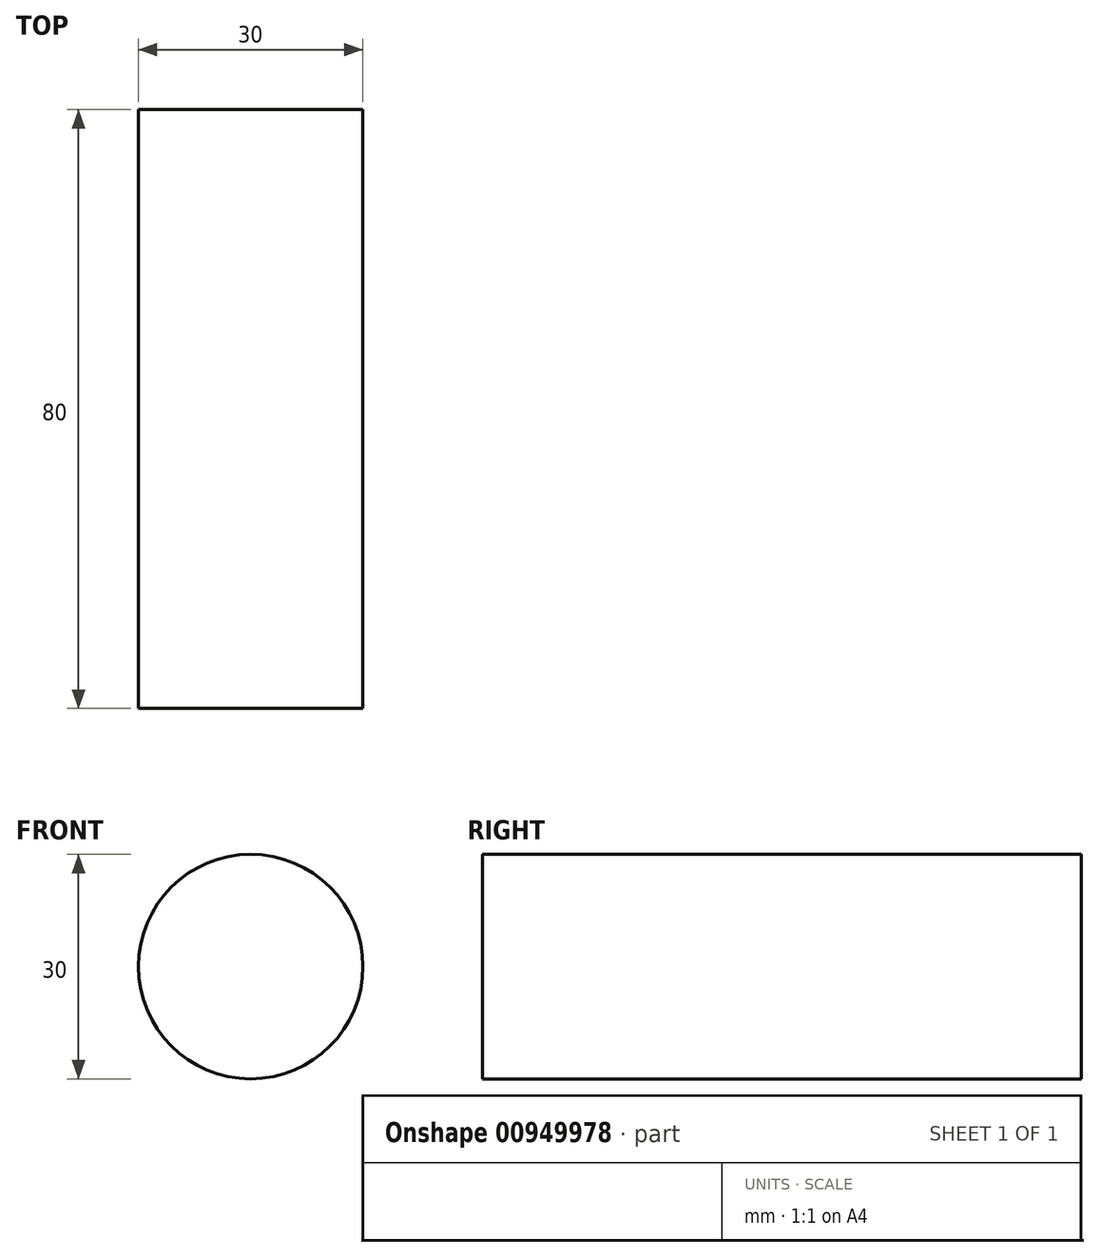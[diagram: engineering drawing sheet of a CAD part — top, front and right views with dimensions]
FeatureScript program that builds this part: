
annotation { "Feature Type Name" : "Feature", "Feature Type Description" : "" }
export const myFeature = defineFeature(function(context is Context, id is Id, definition is map)
    precondition{}
    {
        {
            var Q0;
            Q0=qCreatedBy(makeId("Front.planeOp"),FACE);
            var sketch = newSketch(context, id + "F0", { "sketchPlane" : qUnion([Q0])});
            skCircle(sketch, "E0", {"center": v(0, 0) * mm, "radius": 15 * mm});
            skSolve(sketch);
        }
        {
            var Q0;
            Q0=makeQuery(id+"F0.imprint","IMPRINT",FACE,{"disambiguationData":[TD([[makeQuery(id+"F0.imprint","IMPRINT",EDGE,{"derivedFrom":sQuery(id+"F0.wireOp",EDGE,"E0")}),1.0]])]});
            extrude(context, id + "F1", {"entities" : qUnion([Q0]), "depth" : 80 * mm, "offsetDistance" : 25 * mm});
        }
    });
